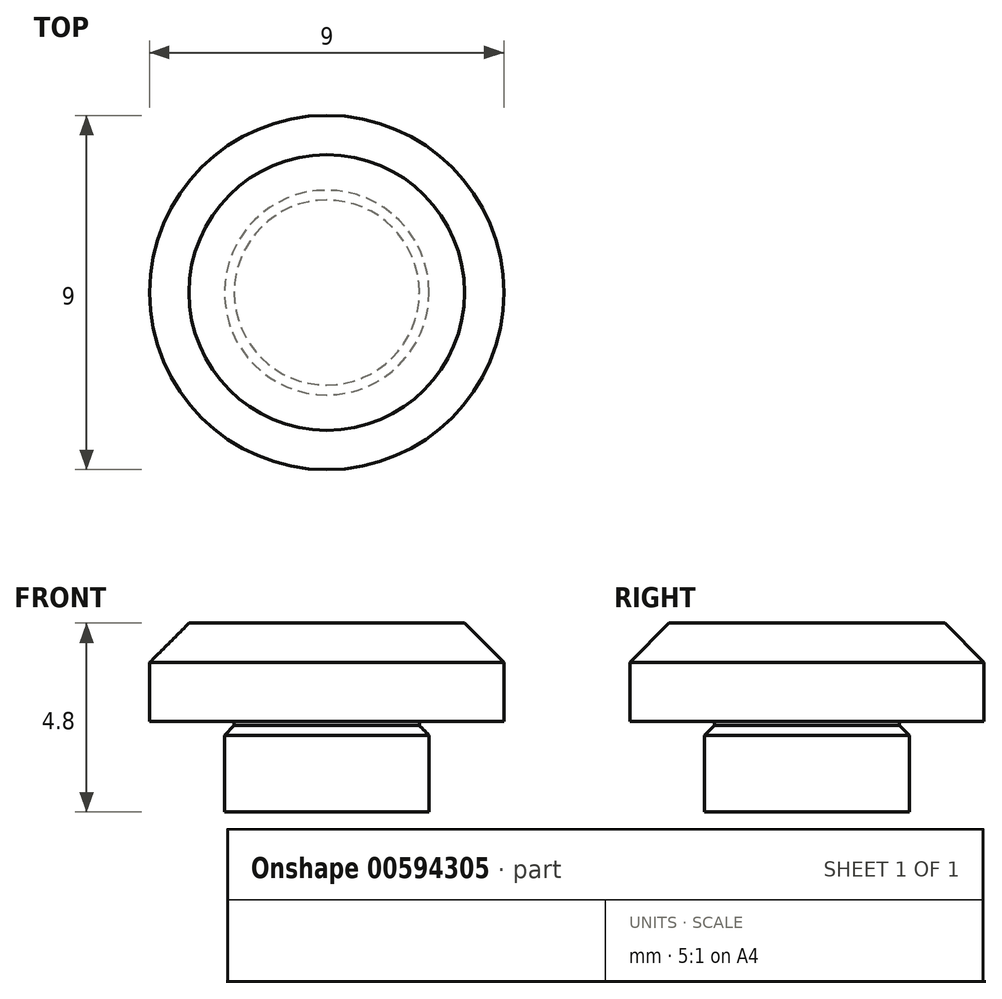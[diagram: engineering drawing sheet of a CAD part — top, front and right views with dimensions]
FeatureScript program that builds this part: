
annotation { "Feature Type Name" : "Feature", "Feature Type Description" : "" }
export const myFeature = defineFeature(function(context is Context, id is Id, definition is map)
    precondition{}
    {
        {
            var Q0;
            Q0=qCreatedBy(makeId("Front.planeOp"),FACE);
            var sketch = newSketch(context, id + "F0", { "sketchPlane" : qUnion([Q0])});
            skLineSegment(sketch, "E0", {"start": v(0, 0) * mm, "end": v(2.6, 0) * mm});
            skLineSegment(sketch, "E1", {"start": v(2.6, 0) * mm, "end": v(2.6, 2.2) * mm});
            skLineSegment(sketch, "E2", {"start": v(2.6, 2.3) * mm, "end": v(4.5, 2.3) * mm});
            skLineSegment(sketch, "E3", {"start": v(4.5, 2.3) * mm, "end": v(4.5, 5.16) * mm});
            skLineSegment(sketch, "E4", {"start": v(4.5, 4.8) * mm, "end": v(4.5, 5.16) * mm});
            skLineSegment(sketch, "E5", {"start": v(4.5, 4.8) * mm, "end": v(0, 4.8) * mm});
            skLineSegment(sketch, "E6", {"start": v(0, 4.8) * mm, "end": v(0, 0) * mm});
            skLineSegment(sketch, "E7", {"start": v(2.35, 2.2) * mm, "end": v(2.6, 2.2) * mm});
            skLineSegment(sketch, "E8", {"start": v(2.6, 2.3) * mm, "end": v(2.35, 2.3) * mm});
            skLineSegment(sketch, "E9", {"start": v(2.35, 2.3) * mm, "end": v(2.35, 2.2) * mm});
            skSolve(sketch);
        }
        {
            var Q0;
            Q0=makeQuery(id+"F0.imprint","IMPRINT",FACE,{"disambiguationData":[TD([[makeQuery(id+"F0.imprint","IMPRINT",EDGE,{"derivedFrom":sQuery(id+"F0.wireOp",EDGE,"E0")}),1.0]])]});
            var Q1;
            Q1=sQuery(id+"F0.wireOp",EDGE,"E6");
            revolve(context, id + "F1", {"entities" : qUnion([Q0]), "axis" : qUnion([Q1]), "revolveType" : RevolveType.FULL});
        }
        {
            var Q0;
            Q0=makeQuery(id+"F1.opRevolve","SWEPT_EDGE",EDGE,{"disambiguationData":[OSD([sQuery(id+"F0.wireOp",EDGE,"E4"),sQuery(id+"F0.wireOp",EDGE,"E5")])]});
            chamfer(context, id + "F2", {"entities" : qUnion([Q0]), "width" : 1 * mm, "tangentPropagation" : true});
        }
        {
            var Q0;
            Q0=makeQuery(id+"F1.opRevolve","SWEPT_EDGE",EDGE,{"disambiguationData":[OSD([sQuery(id+"F0.wireOp",EDGE,"E1"),sQuery(id+"F0.wireOp",EDGE,"E7")])]});
            chamfer(context, id + "F3", {"entities" : qUnion([Q0]), "width" : 0.25 * mm, "tangentPropagation" : true});
        }
    });
